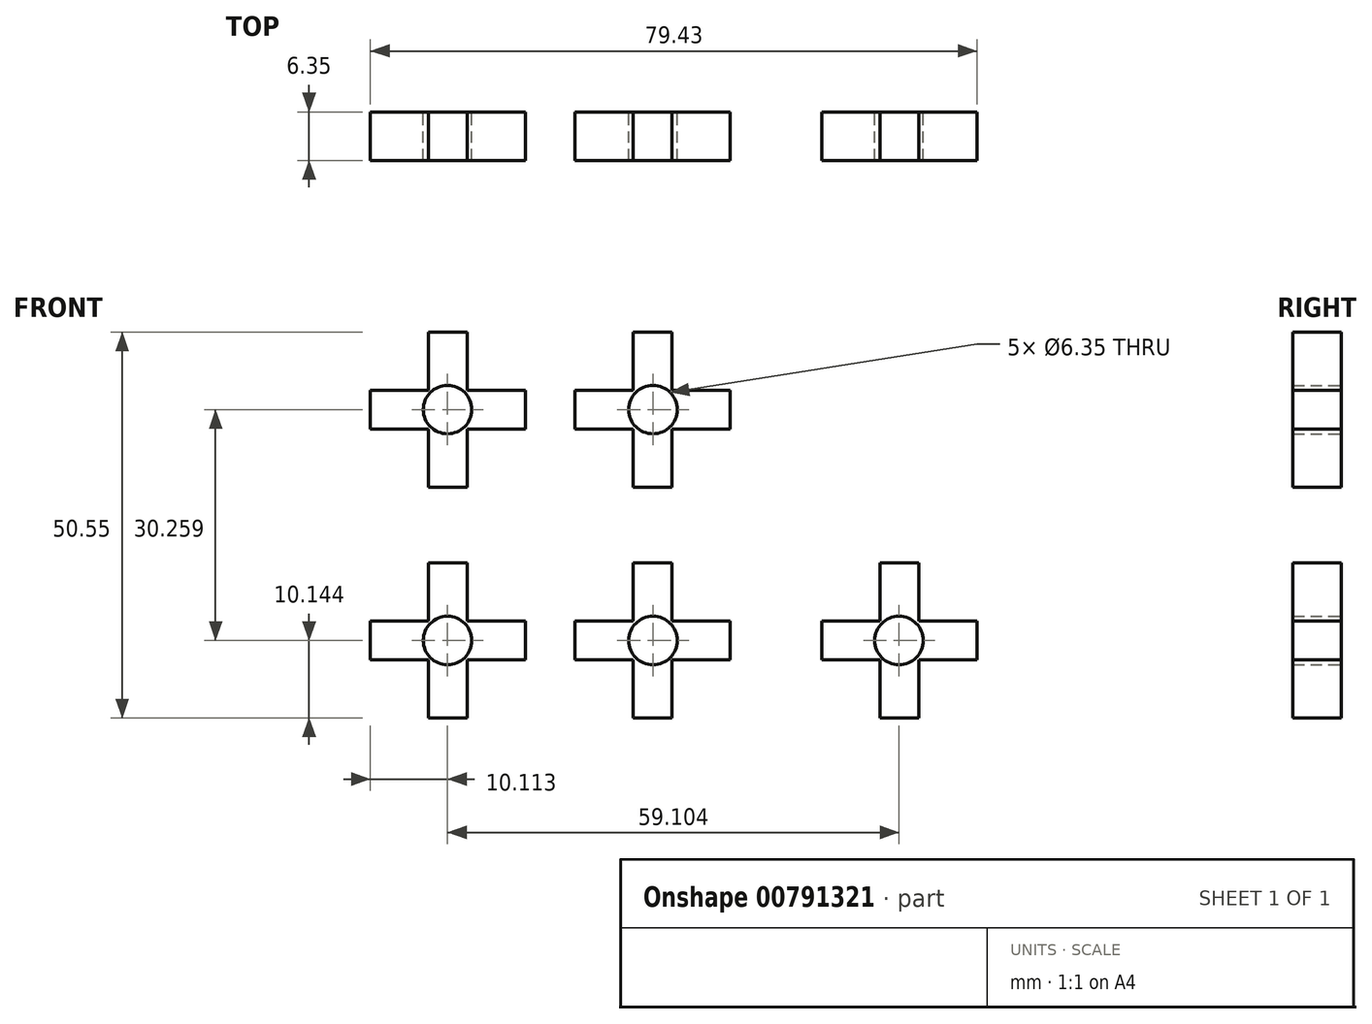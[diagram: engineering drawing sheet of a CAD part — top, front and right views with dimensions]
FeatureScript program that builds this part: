
annotation { "Feature Type Name" : "Feature", "Feature Type Description" : "" }
export const myFeature = defineFeature(function(context is Context, id is Id, definition is map)
    precondition{}
    {
        {
            var Q0;
            Q0=qCreatedBy(makeId("Front.planeOp"),FACE);
            var sketch = newSketch(context, id + "F0", { "sketchPlane" : qUnion([Q0])});
            skLineSegment(sketch, "E0", {"start": v(-62.47, 61.43) * mm, "end": v(-62.47, 53.8) * mm});
            skLineSegment(sketch, "E1", {"start": v(-70.09, 53.8) * mm, "end": v(-62.47, 53.8) * mm});
            skLineSegment(sketch, "E2", {"start": v(-70.09, 53.8) * mm, "end": v(-70.09, 48.73) * mm});
            skLineSegment(sketch, "E3", {"start": v(-70.09, 48.73) * mm, "end": v(-62.47, 48.73) * mm});
            skLineSegment(sketch, "E4", {"start": v(-62.47, 48.73) * mm, "end": v(-62.47, 41.1) * mm});
            skLineSegment(sketch, "E5", {"start": v(-62.47, 41.1) * mm, "end": v(-57.39, 41.1) * mm});
            skLineSegment(sketch, "E6", {"start": v(-57.39, 41.1) * mm, "end": v(-57.39, 48.73) * mm});
            skLineSegment(sketch, "E7", {"start": v(-57.39, 48.73) * mm, "end": v(-49.77, 48.73) * mm});
            skLineSegment(sketch, "E8", {"start": v(-49.77, 48.73) * mm, "end": v(-49.77, 53.8) * mm});
            skLineSegment(sketch, "E9", {"start": v(-49.77, 53.8) * mm, "end": v(-57.39, 53.8) * mm});
            skLineSegment(sketch, "E10", {"start": v(-57.39, 53.8) * mm, "end": v(-57.39, 61.43) * mm});
            skLineSegment(sketch, "E11", {"start": v(-57.39, 61.43) * mm, "end": v(-62.47, 61.43) * mm});
            skCircle(sketch, "E12", {"center": v(-59.98, 51.28) * mm, "radius": 3.18 * mm});
            skLineSegment(sketch, "E13", {"start": v(-46.53, 68.22) * mm, "end": v(-46.53, 9.43) * mm});
            skLineSegment(sketch, "E14.MirrorCS", {"start": v(-43.29, 48.73) * mm, "end": v(-43.29, 53.8) * mm});
            skLineSegment(sketch, "E15.MirrorCS", {"start": v(-35.67, 48.73) * mm, "end": v(-43.29, 48.73) * mm});
            skCircle(sketch, "E16.MirrorC", {"center": v(-33.08, 51.28) * mm, "radius": 3.18 * mm});
            skLineSegment(sketch, "E17.MirrorCS", {"start": v(-35.67, 41.1) * mm, "end": v(-35.67, 48.73) * mm});
            skLineSegment(sketch, "E18.MirrorCS", {"start": v(-30.59, 41.1) * mm, "end": v(-35.67, 41.1) * mm});
            skLineSegment(sketch, "E19.MirrorCS", {"start": v(-30.59, 48.73) * mm, "end": v(-30.59, 41.1) * mm});
            skLineSegment(sketch, "E20.MirrorCS", {"start": v(-22.97, 53.8) * mm, "end": v(-30.59, 53.8) * mm});
            skLineSegment(sketch, "E21.MirrorCS", {"start": v(-22.97, 53.8) * mm, "end": v(-22.97, 48.73) * mm});
            skLineSegment(sketch, "E22.MirrorCS", {"start": v(-22.97, 48.73) * mm, "end": v(-30.59, 48.73) * mm});
            skLineSegment(sketch, "E23.MirrorCS", {"start": v(-30.59, 61.43) * mm, "end": v(-30.59, 53.8) * mm});
            skLineSegment(sketch, "E24.MirrorCS", {"start": v(-35.67, 53.8) * mm, "end": v(-35.67, 61.43) * mm});
            skLineSegment(sketch, "E25.MirrorCS", {"start": v(-35.67, 61.43) * mm, "end": v(-30.59, 61.43) * mm});
            skLineSegment(sketch, "E26.MirrorCS", {"start": v(-43.29, 53.8) * mm, "end": v(-35.67, 53.8) * mm});
            skLineSegment(sketch, "E27", {"start": v(-73.57, 36.15) * mm, "end": v(-16.98, 36.15) * mm});
            skLineSegment(sketch, "E28.MirrorCS", {"start": v(-35.67, 31.2) * mm, "end": v(-35.67, 23.58) * mm});
            skLineSegment(sketch, "E29.MirrorCS", {"start": v(-30.59, 31.2) * mm, "end": v(-35.67, 31.2) * mm});
            skCircle(sketch, "E30.MirrorC", {"center": v(-33.08, 21.02) * mm, "radius": 3.18 * mm});
            skLineSegment(sketch, "E31.MirrorCS", {"start": v(-43.29, 18.5) * mm, "end": v(-35.67, 18.5) * mm});
            skLineSegment(sketch, "E32.MirrorCS", {"start": v(-43.29, 23.58) * mm, "end": v(-43.29, 18.5) * mm});
            skLineSegment(sketch, "E33.MirrorCS", {"start": v(-35.67, 23.58) * mm, "end": v(-43.29, 23.58) * mm});
            skLineSegment(sketch, "E34.MirrorCS", {"start": v(-22.97, 23.58) * mm, "end": v(-30.59, 23.58) * mm});
            skLineSegment(sketch, "E35.MirrorCS", {"start": v(-22.97, 18.5) * mm, "end": v(-30.59, 18.5) * mm});
            skLineSegment(sketch, "E36.MirrorCS", {"start": v(-30.59, 10.88) * mm, "end": v(-30.59, 18.5) * mm});
            skLineSegment(sketch, "E37.MirrorCS", {"start": v(-35.67, 18.5) * mm, "end": v(-35.67, 10.88) * mm});
            skLineSegment(sketch, "E38.MirrorCS", {"start": v(-35.67, 10.88) * mm, "end": v(-30.59, 10.88) * mm});
            skLineSegment(sketch, "E39.MirrorCS", {"start": v(-30.59, 23.58) * mm, "end": v(-30.59, 31.2) * mm});
            skLineSegment(sketch, "E40.MirrorCS", {"start": v(-22.97, 18.5) * mm, "end": v(-22.97, 23.58) * mm});
            skLineSegment(sketch, "E41.MirrorCS", {"start": v(-49.77, 23.58) * mm, "end": v(-49.77, 18.5) * mm});
            skLineSegment(sketch, "E42.MirrorCS", {"start": v(-49.77, 18.5) * mm, "end": v(-57.39, 18.5) * mm});
            skLineSegment(sketch, "E43.MirrorCS", {"start": v(-57.39, 18.5) * mm, "end": v(-57.39, 10.88) * mm});
            skLineSegment(sketch, "E44.MirrorCS", {"start": v(-57.39, 10.88) * mm, "end": v(-62.47, 10.88) * mm});
            skLineSegment(sketch, "E45.MirrorCS", {"start": v(-62.47, 10.88) * mm, "end": v(-62.47, 18.5) * mm});
            skLineSegment(sketch, "E46.MirrorCS", {"start": v(-70.09, 18.5) * mm, "end": v(-62.47, 18.5) * mm});
            skLineSegment(sketch, "E47.MirrorCS", {"start": v(-70.09, 18.5) * mm, "end": v(-70.09, 23.58) * mm});
            skLineSegment(sketch, "E48.MirrorCS", {"start": v(-70.09, 23.58) * mm, "end": v(-62.47, 23.58) * mm});
            skLineSegment(sketch, "E49.MirrorCS", {"start": v(-62.47, 23.58) * mm, "end": v(-62.47, 31.2) * mm});
            skLineSegment(sketch, "E50.MirrorCS", {"start": v(-62.47, 31.2) * mm, "end": v(-57.39, 31.2) * mm});
            skLineSegment(sketch, "E51.MirrorCS", {"start": v(-57.39, 31.2) * mm, "end": v(-57.39, 23.58) * mm});
            skCircle(sketch, "E52.MirrorC", {"center": v(-59.98, 21.02) * mm, "radius": 3.18 * mm});
            skLineSegment(sketch, "E53.MirrorCS", {"start": v(-57.39, 23.58) * mm, "end": v(-49.77, 23.58) * mm});
            skLineSegment(sketch, "E54", {"start": v(-16.98, 36.15) * mm, "end": v(-16.98, 0) * mm});
            skLineSegment(sketch, "E55.MirrorCS", {"start": v(-10.98, 18.5) * mm, "end": v(-10.98, 23.58) * mm});
            skLineSegment(sketch, "E56.MirrorCS", {"start": v(-10.98, 23.58) * mm, "end": v(-3.36, 23.58) * mm});
            skLineSegment(sketch, "E57.MirrorCS", {"start": v(1.72, 31.2) * mm, "end": v(1.72, 23.58) * mm});
            skLineSegment(sketch, "E58.MirrorCS", {"start": v(-3.36, 31.2) * mm, "end": v(1.72, 31.2) * mm});
            skLineSegment(sketch, "E59.MirrorCS", {"start": v(9.34, 18.5) * mm, "end": v(1.72, 18.5) * mm});
            skLineSegment(sketch, "E60.MirrorCS", {"start": v(9.34, 23.58) * mm, "end": v(9.34, 18.5) * mm});
            skLineSegment(sketch, "E61.MirrorCS", {"start": v(1.72, 18.5) * mm, "end": v(1.72, 10.88) * mm});
            skLineSegment(sketch, "E62.MirrorCS", {"start": v(1.72, 10.88) * mm, "end": v(-3.36, 10.88) * mm});
            skLineSegment(sketch, "E63.MirrorCS", {"start": v(-3.36, 10.88) * mm, "end": v(-3.36, 18.5) * mm});
            skLineSegment(sketch, "E64.MirrorCS", {"start": v(-10.98, 18.5) * mm, "end": v(-3.36, 18.5) * mm});
            skLineSegment(sketch, "E65.MirrorCS", {"start": v(-3.36, 23.58) * mm, "end": v(-3.36, 31.2) * mm});
            skCircle(sketch, "E66.MirrorC", {"center": v(-0.87, 21.02) * mm, "radius": 3.18 * mm});
            skLineSegment(sketch, "E67.MirrorCS", {"start": v(1.72, 23.58) * mm, "end": v(9.34, 23.58) * mm});
            skSolve(sketch);
        }
        {
            var Q0;
            Q0=makeQuery(id+"F0.imprint","IMPRINT",FACE,{"disambiguationData":[TD([[makeQuery(id+"F0.imprint","IMPRINT",EDGE,{"derivedFrom":sQuery(id+"F0.wireOp",EDGE,"E0")}),1.0]])]});
            extrude(context, id + "F1", {"entities" : qUnion([Q0]), "depth" : 6.35 * mm, "offsetDistance" : 25.4 * mm});
        }
        {
            var Q0;
            Q0=makeQuery(id+"F0.imprint","IMPRINT",FACE,{"disambiguationData":[TD([[makeQuery(id+"F0.imprint","IMPRINT",EDGE,{"derivedFrom":sQuery(id+"F0.wireOp",EDGE,"E14.MirrorCS")}),-1.0]])]});
            var Q1;
            Q1=makeQuery(id+"F0.imprint","IMPRINT",FACE,{"disambiguationData":[TD([[makeQuery(id+"F0.imprint","IMPRINT",EDGE,{"derivedFrom":sQuery(id+"F0.wireOp",EDGE,"E41.MirrorCS")}),-1.0]])]});
            var Q2;
            Q2=makeQuery(id+"F0.imprint","IMPRINT",FACE,{"disambiguationData":[TD([[makeQuery(id+"F0.imprint","IMPRINT",EDGE,{"derivedFrom":sQuery(id+"F0.wireOp",EDGE,"E28.MirrorCS")}),1.0]])]});
            var Q3;
            Q3=makeQuery(id+"F0.imprint","IMPRINT",FACE,{"disambiguationData":[TD([[makeQuery(id+"F0.imprint","IMPRINT",EDGE,{"derivedFrom":sQuery(id+"F0.wireOp",EDGE,"E55.MirrorCS")}),-1.0]])]});
            extrude(context, id + "F2", {"entities" : qUnion([Q0, Q1, Q2, Q3]), "depth" : 6.35 * mm, "offsetDistance" : 25.4 * mm});
        }
    });
